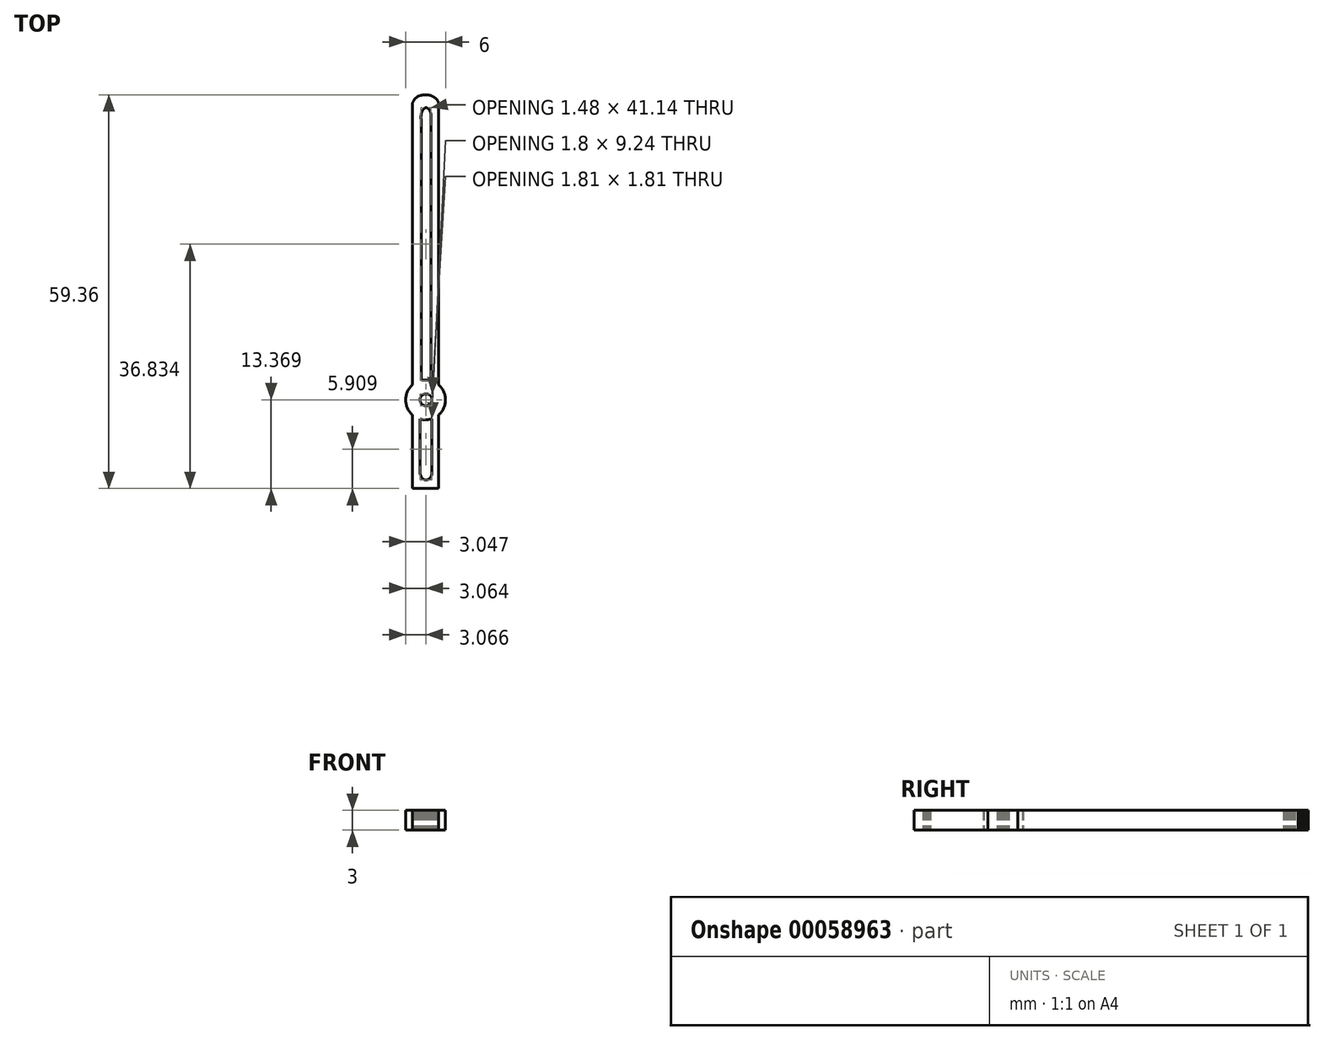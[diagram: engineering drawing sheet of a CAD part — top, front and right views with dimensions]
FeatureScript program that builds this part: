
annotation { "Feature Type Name" : "Feature", "Feature Type Description" : "" }
export const myFeature = defineFeature(function(context is Context, id is Id, definition is map)
    precondition{}
    {
        {
            var Q0;
            Q0=qCreatedBy(makeId("Top.planeOp"),FACE);
            var sketch = newSketch(context, id + "F0", { "sketchPlane" : qUnion([Q0])});
            skLineSegment(sketch, "E0", {"start": v(-1.98, 12.81) * mm, "end": v(-1.98, 28.31) * mm});
            skLineSegment(sketch, "E1", {"start": v(-1.98, 28.31) * mm, "end": v(-1.97, 28.38) * mm});
            skLineSegment(sketch, "E2", {"start": v(-1.97, 28.38) * mm, "end": v(-1.96, 28.45) * mm});
            skLineSegment(sketch, "E3", {"start": v(-1.96, 28.45) * mm, "end": v(-1.94, 28.52) * mm});
            skLineSegment(sketch, "E4", {"start": v(-1.94, 28.52) * mm, "end": v(-1.91, 28.59) * mm});
            skLineSegment(sketch, "E5", {"start": v(-1.91, 28.59) * mm, "end": v(-1.89, 28.65) * mm});
            skLineSegment(sketch, "E6", {"start": v(-1.89, 28.65) * mm, "end": v(-1.86, 28.72) * mm});
            skLineSegment(sketch, "E7", {"start": v(-1.86, 28.72) * mm, "end": v(-1.82, 28.78) * mm});
            skLineSegment(sketch, "E8", {"start": v(-1.82, 28.78) * mm, "end": v(-1.78, 28.85) * mm});
            skLineSegment(sketch, "E9", {"start": v(-1.78, 28.85) * mm, "end": v(-1.74, 28.9) * mm});
            skLineSegment(sketch, "E10", {"start": v(-1.74, 28.9) * mm, "end": v(-1.7, 28.96) * mm});
            skLineSegment(sketch, "E11", {"start": v(-1.7, 28.96) * mm, "end": v(-1.65, 29.02) * mm});
            skLineSegment(sketch, "E12", {"start": v(-1.65, 29.02) * mm, "end": v(-1.6, 29.08) * mm});
            skLineSegment(sketch, "E13", {"start": v(-1.6, 29.08) * mm, "end": v(-1.54, 29.13) * mm});
            skLineSegment(sketch, "E14", {"start": v(-1.54, 29.13) * mm, "end": v(-1.48, 29.18) * mm});
            skLineSegment(sketch, "E15", {"start": v(-1.48, 29.18) * mm, "end": v(-1.42, 29.23) * mm});
            skLineSegment(sketch, "E16", {"start": v(-1.42, 29.23) * mm, "end": v(-1.35, 29.28) * mm});
            skLineSegment(sketch, "E17", {"start": v(-1.35, 29.28) * mm, "end": v(-1.28, 29.32) * mm});
            skLineSegment(sketch, "E18", {"start": v(-1.28, 29.32) * mm, "end": v(-1.21, 29.37) * mm});
            skLineSegment(sketch, "E19", {"start": v(-1.21, 29.37) * mm, "end": v(-1.07, 29.44) * mm});
            skLineSegment(sketch, "E20", {"start": v(-1.07, 29.44) * mm, "end": v(-0.9, 29.51) * mm});
            skLineSegment(sketch, "E21", {"start": v(-0.9, 29.51) * mm, "end": v(-0.74, 29.57) * mm});
            skLineSegment(sketch, "E22", {"start": v(-0.74, 29.57) * mm, "end": v(-0.57, 29.62) * mm});
            skLineSegment(sketch, "E23", {"start": v(-0.57, 29.62) * mm, "end": v(-0.48, 29.63) * mm});
            skLineSegment(sketch, "E24", {"start": v(-0.48, 29.63) * mm, "end": v(-0.38, 29.65) * mm});
            skLineSegment(sketch, "E25", {"start": v(-0.38, 29.65) * mm, "end": v(-0.3, 29.66) * mm});
            skLineSegment(sketch, "E26", {"start": v(-0.3, 29.66) * mm, "end": v(-0.2, 29.67) * mm});
            skLineSegment(sketch, "E27", {"start": v(-0.2, 29.67) * mm, "end": v(-0.1, 29.67) * mm});
            skLineSegment(sketch, "E28", {"start": v(-0.1, 29.67) * mm, "end": v(0, 29.68) * mm});
            skLineSegment(sketch, "E29", {"start": v(0, 29.68) * mm, "end": v(0.1, 29.67) * mm});
            skLineSegment(sketch, "E30", {"start": v(0.1, 29.67) * mm, "end": v(0.2, 29.67) * mm});
            skLineSegment(sketch, "E31", {"start": v(0.2, 29.67) * mm, "end": v(0.3, 29.66) * mm});
            skLineSegment(sketch, "E32", {"start": v(0.3, 29.66) * mm, "end": v(0.4, 29.65) * mm});
            skLineSegment(sketch, "E33", {"start": v(0.4, 29.65) * mm, "end": v(0.5, 29.63) * mm});
            skLineSegment(sketch, "E34", {"start": v(0.5, 29.63) * mm, "end": v(0.59, 29.6) * mm});
            skLineSegment(sketch, "E35", {"start": v(0.59, 29.6) * mm, "end": v(0.68, 29.59) * mm});
            skLineSegment(sketch, "E36", {"start": v(0.68, 29.59) * mm, "end": v(0.77, 29.56) * mm});
            skLineSegment(sketch, "E37", {"start": v(0.77, 29.56) * mm, "end": v(0.86, 29.53) * mm});
            skLineSegment(sketch, "E38", {"start": v(0.86, 29.53) * mm, "end": v(0.94, 29.5) * mm});
            skLineSegment(sketch, "E39", {"start": v(0.94, 29.5) * mm, "end": v(1.02, 29.46) * mm});
            skLineSegment(sketch, "E40", {"start": v(1.02, 29.46) * mm, "end": v(1.1, 29.42) * mm});
            skLineSegment(sketch, "E41", {"start": v(1.1, 29.42) * mm, "end": v(1.18, 29.38) * mm});
            skLineSegment(sketch, "E42", {"start": v(1.18, 29.38) * mm, "end": v(1.26, 29.33) * mm});
            skLineSegment(sketch, "E43", {"start": v(1.26, 29.33) * mm, "end": v(1.33, 29.29) * mm});
            skLineSegment(sketch, "E44", {"start": v(1.33, 29.29) * mm, "end": v(1.4, 29.24) * mm});
            skLineSegment(sketch, "E45", {"start": v(1.4, 29.24) * mm, "end": v(1.46, 29.19) * mm});
            skLineSegment(sketch, "E46", {"start": v(1.46, 29.19) * mm, "end": v(1.53, 29.13) * mm});
            skLineSegment(sketch, "E47", {"start": v(1.53, 29.13) * mm, "end": v(1.59, 29.08) * mm});
            skLineSegment(sketch, "E48", {"start": v(1.59, 29.08) * mm, "end": v(1.64, 29.02) * mm});
            skLineSegment(sketch, "E49", {"start": v(1.64, 29.02) * mm, "end": v(1.7, 28.96) * mm});
            skLineSegment(sketch, "E50", {"start": v(1.7, 28.96) * mm, "end": v(1.74, 28.9) * mm});
            skLineSegment(sketch, "E51", {"start": v(1.74, 28.9) * mm, "end": v(1.78, 28.83) * mm});
            skLineSegment(sketch, "E52", {"start": v(1.78, 28.83) * mm, "end": v(1.82, 28.76) * mm});
            skLineSegment(sketch, "E53", {"start": v(1.82, 28.76) * mm, "end": v(1.86, 28.7) * mm});
            skLineSegment(sketch, "E54", {"start": v(1.86, 28.7) * mm, "end": v(1.9, 28.63) * mm});
            skLineSegment(sketch, "E55", {"start": v(1.9, 28.63) * mm, "end": v(1.92, 28.56) * mm});
            skLineSegment(sketch, "E56", {"start": v(1.92, 28.56) * mm, "end": v(1.94, 28.48) * mm});
            skLineSegment(sketch, "E57", {"start": v(1.94, 28.48) * mm, "end": v(1.96, 28.4) * mm});
            skLineSegment(sketch, "E58", {"start": v(1.96, 28.4) * mm, "end": v(1.97, 28.33) * mm});
            skLineSegment(sketch, "E59", {"start": v(1.97, 28.33) * mm, "end": v(1.98, 28.26) * mm});
            skLineSegment(sketch, "E60", {"start": v(1.98, 28.26) * mm, "end": v(1.98, 28.18) * mm});
            skLineSegment(sketch, "E61", {"start": v(1.98, 28.18) * mm, "end": v(1.98, 28.12) * mm});
            skLineSegment(sketch, "E62", {"start": v(1.98, 28.12) * mm, "end": v(1.98, 12.81) * mm});
            skLineSegment(sketch, "E63", {"start": v(1.98, 12.81) * mm, "end": v(1.98, 5.29) * mm});
            skLineSegment(sketch, "E64", {"start": v(1.98, 5.29) * mm, "end": v(1.98, -7) * mm});
            skLineSegment(sketch, "E65", {"start": v(1.98, -7) * mm, "end": v(1.98, -16.31) * mm});
            skLineSegment(sketch, "E66", {"start": v(1.98, -16.31) * mm, "end": v(1.98, -18.16) * mm});
            skLineSegment(sketch, "E67", {"start": v(1.98, -18.16) * mm, "end": v(1.98, -29.68) * mm});
            skLineSegment(sketch, "E68", {"start": v(1.98, -29.68) * mm, "end": v(-1.98, -29.68) * mm});
            skLineSegment(sketch, "E69", {"start": v(-1.98, -29.68) * mm, "end": v(-1.98, -18.16) * mm});
            skLineSegment(sketch, "E70", {"start": v(-1.98, -18.16) * mm, "end": v(-1.98, -16.31) * mm});
            skLineSegment(sketch, "E71", {"start": v(-1.98, -16.31) * mm, "end": v(-1.98, -7) * mm});
            skLineSegment(sketch, "E72", {"start": v(-1.98, -7) * mm, "end": v(-1.98, 5.26) * mm});
            skLineSegment(sketch, "E73", {"start": v(-1.98, 5.26) * mm, "end": v(-1.98, 12.81) * mm});
            skLineSegment(sketch, "E74", {"start": v(0.97, -16.31) * mm, "end": v(0.97, -16.25) * mm});
            skLineSegment(sketch, "E75", {"start": v(0.97, -16.25) * mm, "end": v(0.96, -16.2) * mm});
            skLineSegment(sketch, "E76", {"start": v(0.96, -16.2) * mm, "end": v(0.95, -16.14) * mm});
            skLineSegment(sketch, "E77", {"start": v(0.95, -16.14) * mm, "end": v(0.94, -16.09) * mm});
            skLineSegment(sketch, "E78", {"start": v(0.94, -16.09) * mm, "end": v(0.93, -16.03) * mm});
            skLineSegment(sketch, "E79", {"start": v(0.93, -16.03) * mm, "end": v(0.9, -15.98) * mm});
            skLineSegment(sketch, "E80", {"start": v(0.9, -15.98) * mm, "end": v(0.88, -15.93) * mm});
            skLineSegment(sketch, "E81", {"start": v(0.88, -15.93) * mm, "end": v(0.86, -15.88) * mm});
            skLineSegment(sketch, "E82", {"start": v(0.86, -15.88) * mm, "end": v(0.83, -15.83) * mm});
            skLineSegment(sketch, "E83", {"start": v(0.83, -15.83) * mm, "end": v(0.8, -15.78) * mm});
            skLineSegment(sketch, "E84", {"start": v(0.8, -15.78) * mm, "end": v(0.76, -15.74) * mm});
            skLineSegment(sketch, "E85", {"start": v(0.76, -15.74) * mm, "end": v(0.72, -15.7) * mm});
            skLineSegment(sketch, "E86", {"start": v(0.72, -15.7) * mm, "end": v(0.68, -15.65) * mm});
            skLineSegment(sketch, "E87", {"start": v(0.68, -15.65) * mm, "end": v(0.64, -15.61) * mm});
            skLineSegment(sketch, "E88", {"start": v(0.64, -15.61) * mm, "end": v(0.6, -15.58) * mm});
            skLineSegment(sketch, "E89", {"start": v(0.6, -15.58) * mm, "end": v(0.55, -15.55) * mm});
            skLineSegment(sketch, "E90", {"start": v(0.55, -15.55) * mm, "end": v(0.5, -15.52) * mm});
            skLineSegment(sketch, "E91", {"start": v(0.5, -15.52) * mm, "end": v(0.45, -15.5) * mm});
            skLineSegment(sketch, "E92", {"start": v(0.45, -15.5) * mm, "end": v(0.4, -15.47) * mm});
            skLineSegment(sketch, "E93", {"start": v(0.4, -15.47) * mm, "end": v(0.35, -15.45) * mm});
            skLineSegment(sketch, "E94", {"start": v(0.35, -15.45) * mm, "end": v(0.3, -15.44) * mm});
            skLineSegment(sketch, "E95", {"start": v(0.3, -15.44) * mm, "end": v(0.24, -15.42) * mm});
            skLineSegment(sketch, "E96", {"start": v(0.24, -15.42) * mm, "end": v(0.18, -15.41) * mm});
            skLineSegment(sketch, "E97", {"start": v(0.18, -15.41) * mm, "end": v(0.12, -15.4) * mm});
            skLineSegment(sketch, "E98", {"start": v(0.12, -15.4) * mm, "end": v(0.07, -15.4) * mm});
            skLineSegment(sketch, "E99", {"start": v(0.07, -15.4) * mm, "end": v(0, -15.4) * mm});
            skLineSegment(sketch, "E100", {"start": v(0, -15.4) * mm, "end": v(-0.05, -15.41) * mm});
            skLineSegment(sketch, "E101", {"start": v(-0.05, -15.41) * mm, "end": v(-0.1, -15.42) * mm});
            skLineSegment(sketch, "E102", {"start": v(-0.1, -15.42) * mm, "end": v(-0.16, -15.43) * mm});
            skLineSegment(sketch, "E103", {"start": v(-0.16, -15.43) * mm, "end": v(-0.21, -15.45) * mm});
            skLineSegment(sketch, "E104", {"start": v(-0.21, -15.45) * mm, "end": v(-0.27, -15.47) * mm});
            skLineSegment(sketch, "E105", {"start": v(-0.27, -15.47) * mm, "end": v(-0.32, -15.5) * mm});
            skLineSegment(sketch, "E106", {"start": v(-0.32, -15.5) * mm, "end": v(-0.37, -15.52) * mm});
            skLineSegment(sketch, "E107", {"start": v(-0.37, -15.52) * mm, "end": v(-0.42, -15.55) * mm});
            skLineSegment(sketch, "E108", {"start": v(-0.42, -15.55) * mm, "end": v(-0.46, -15.58) * mm});
            skLineSegment(sketch, "E109", {"start": v(-0.46, -15.58) * mm, "end": v(-0.5, -15.61) * mm});
            skLineSegment(sketch, "E110", {"start": v(-0.5, -15.61) * mm, "end": v(-0.55, -15.65) * mm});
            skLineSegment(sketch, "E111", {"start": v(-0.55, -15.65) * mm, "end": v(-0.6, -15.69) * mm});
            skLineSegment(sketch, "E112", {"start": v(-0.6, -15.69) * mm, "end": v(-0.63, -15.73) * mm});
            skLineSegment(sketch, "E113", {"start": v(-0.63, -15.73) * mm, "end": v(-0.67, -15.78) * mm});
            skLineSegment(sketch, "E114", {"start": v(-0.67, -15.78) * mm, "end": v(-0.7, -15.82) * mm});
            skLineSegment(sketch, "E115", {"start": v(-0.7, -15.82) * mm, "end": v(-0.73, -15.87) * mm});
            skLineSegment(sketch, "E116", {"start": v(-0.73, -15.87) * mm, "end": v(-0.75, -15.92) * mm});
            skLineSegment(sketch, "E117", {"start": v(-0.75, -15.92) * mm, "end": v(-0.78, -15.97) * mm});
            skLineSegment(sketch, "E118", {"start": v(-0.78, -15.97) * mm, "end": v(-0.8, -16.03) * mm});
            skLineSegment(sketch, "E119", {"start": v(-0.8, -16.03) * mm, "end": v(-0.81, -16.08) * mm});
            skLineSegment(sketch, "E120", {"start": v(-0.81, -16.08) * mm, "end": v(-0.82, -16.14) * mm});
            skLineSegment(sketch, "E121", {"start": v(-0.82, -16.14) * mm, "end": v(-0.83, -16.2) * mm});
            skLineSegment(sketch, "E122", {"start": v(-0.83, -16.2) * mm, "end": v(-0.84, -16.25) * mm});
            skLineSegment(sketch, "E123", {"start": v(-0.84, -16.25) * mm, "end": v(-0.84, -16.3) * mm});
            skLineSegment(sketch, "E124", {"start": v(-0.84, -16.3) * mm, "end": v(-0.84, -16.36) * mm});
            skLineSegment(sketch, "E125", {"start": v(-0.84, -16.36) * mm, "end": v(-0.83, -16.42) * mm});
            skLineSegment(sketch, "E126", {"start": v(-0.83, -16.42) * mm, "end": v(-0.83, -16.48) * mm});
            skLineSegment(sketch, "E127", {"start": v(-0.83, -16.48) * mm, "end": v(-0.81, -16.53) * mm});
            skLineSegment(sketch, "E128", {"start": v(-0.81, -16.53) * mm, "end": v(-0.8, -16.59) * mm});
            skLineSegment(sketch, "E129", {"start": v(-0.8, -16.59) * mm, "end": v(-0.78, -16.64) * mm});
            skLineSegment(sketch, "E130", {"start": v(-0.78, -16.64) * mm, "end": v(-0.76, -16.7) * mm});
            skLineSegment(sketch, "E131", {"start": v(-0.76, -16.7) * mm, "end": v(-0.73, -16.74) * mm});
            skLineSegment(sketch, "E132", {"start": v(-0.73, -16.74) * mm, "end": v(-0.7, -16.8) * mm});
            skLineSegment(sketch, "E133", {"start": v(-0.7, -16.8) * mm, "end": v(-0.67, -16.84) * mm});
            skLineSegment(sketch, "E134", {"start": v(-0.67, -16.84) * mm, "end": v(-0.64, -16.88) * mm});
            skLineSegment(sketch, "E135", {"start": v(-0.64, -16.88) * mm, "end": v(-0.6, -16.93) * mm});
            skLineSegment(sketch, "E136", {"start": v(-0.6, -16.93) * mm, "end": v(-0.56, -16.97) * mm});
            skLineSegment(sketch, "E137", {"start": v(-0.56, -16.97) * mm, "end": v(-0.52, -17) * mm});
            skLineSegment(sketch, "E138", {"start": v(-0.52, -17) * mm, "end": v(-0.47, -17.04) * mm});
            skLineSegment(sketch, "E139", {"start": v(-0.47, -17.04) * mm, "end": v(-0.43, -17.07) * mm});
            skLineSegment(sketch, "E140", {"start": v(-0.43, -17.07) * mm, "end": v(-0.38, -17.1) * mm});
            skLineSegment(sketch, "E141", {"start": v(-0.38, -17.1) * mm, "end": v(-0.33, -17.13) * mm});
            skLineSegment(sketch, "E142", {"start": v(-0.33, -17.13) * mm, "end": v(-0.27, -17.15) * mm});
            skLineSegment(sketch, "E143", {"start": v(-0.27, -17.15) * mm, "end": v(-0.22, -17.17) * mm});
            skLineSegment(sketch, "E144", {"start": v(-0.22, -17.17) * mm, "end": v(-0.17, -17.19) * mm});
            skLineSegment(sketch, "E145", {"start": v(-0.17, -17.19) * mm, "end": v(-0.11, -17.2) * mm});
            skLineSegment(sketch, "E146", {"start": v(-0.11, -17.2) * mm, "end": v(-0.06, -17.2) * mm});
            skLineSegment(sketch, "E147", {"start": v(-0.06, -17.2) * mm, "end": v(0, -17.21) * mm});
            skLineSegment(sketch, "E148", {"start": v(0, -17.21) * mm, "end": v(0.06, -17.22) * mm});
            skLineSegment(sketch, "E149", {"start": v(0.06, -17.22) * mm, "end": v(0.11, -17.21) * mm});
            skLineSegment(sketch, "E150", {"start": v(0.11, -17.21) * mm, "end": v(0.17, -17.21) * mm});
            skLineSegment(sketch, "E151", {"start": v(0.17, -17.21) * mm, "end": v(0.23, -17.2) * mm});
            skLineSegment(sketch, "E152", {"start": v(0.23, -17.2) * mm, "end": v(0.28, -17.19) * mm});
            skLineSegment(sketch, "E153", {"start": v(0.28, -17.19) * mm, "end": v(0.34, -17.17) * mm});
            skLineSegment(sketch, "E154", {"start": v(0.34, -17.17) * mm, "end": v(0.4, -17.16) * mm});
            skLineSegment(sketch, "E155", {"start": v(0.4, -17.16) * mm, "end": v(0.44, -17.13) * mm});
            skLineSegment(sketch, "E156", {"start": v(0.44, -17.13) * mm, "end": v(0.5, -17.1) * mm});
            skLineSegment(sketch, "E157", {"start": v(0.5, -17.1) * mm, "end": v(0.54, -17.08) * mm});
            skLineSegment(sketch, "E158", {"start": v(0.54, -17.08) * mm, "end": v(0.6, -17.05) * mm});
            skLineSegment(sketch, "E159", {"start": v(0.6, -17.05) * mm, "end": v(0.64, -17.01) * mm});
            skLineSegment(sketch, "E160", {"start": v(0.64, -17.01) * mm, "end": v(0.68, -16.98) * mm});
            skLineSegment(sketch, "E161", {"start": v(0.68, -16.98) * mm, "end": v(0.72, -16.94) * mm});
            skLineSegment(sketch, "E162", {"start": v(0.72, -16.94) * mm, "end": v(0.76, -16.9) * mm});
            skLineSegment(sketch, "E163", {"start": v(0.76, -16.9) * mm, "end": v(0.8, -16.85) * mm});
            skLineSegment(sketch, "E164", {"start": v(0.8, -16.85) * mm, "end": v(0.82, -16.8) * mm});
            skLineSegment(sketch, "E165", {"start": v(0.82, -16.8) * mm, "end": v(0.85, -16.75) * mm});
            skLineSegment(sketch, "E166", {"start": v(0.85, -16.75) * mm, "end": v(0.88, -16.7) * mm});
            skLineSegment(sketch, "E167", {"start": v(0.88, -16.7) * mm, "end": v(0.9, -16.65) * mm});
            skLineSegment(sketch, "E168", {"start": v(0.9, -16.65) * mm, "end": v(0.92, -16.6) * mm});
            skLineSegment(sketch, "E169", {"start": v(0.92, -16.6) * mm, "end": v(0.94, -16.54) * mm});
            skLineSegment(sketch, "E170", {"start": v(0.94, -16.54) * mm, "end": v(0.95, -16.49) * mm});
            skLineSegment(sketch, "E171", {"start": v(0.95, -16.49) * mm, "end": v(0.96, -16.43) * mm});
            skLineSegment(sketch, "E172", {"start": v(0.96, -16.43) * mm, "end": v(0.97, -16.38) * mm});
            skLineSegment(sketch, "E173", {"start": v(0.97, -16.38) * mm, "end": v(0.97, -16.31) * mm});
            skLineSegment(sketch, "E174", {"start": v(-0.83, -27.22) * mm, "end": v(-0.83, -27.34) * mm});
            skLineSegment(sketch, "E175", {"start": v(-0.83, -27.34) * mm, "end": v(-0.81, -27.46) * mm});
            skLineSegment(sketch, "E176", {"start": v(-0.81, -27.46) * mm, "end": v(-0.8, -27.57) * mm});
            skLineSegment(sketch, "E177", {"start": v(-0.8, -27.57) * mm, "end": v(-0.76, -27.68) * mm});
            skLineSegment(sketch, "E178", {"start": v(-0.76, -27.68) * mm, "end": v(-0.72, -27.78) * mm});
            skLineSegment(sketch, "E179", {"start": v(-0.72, -27.78) * mm, "end": v(-0.68, -27.87) * mm});
            skLineSegment(sketch, "E180", {"start": v(-0.68, -27.87) * mm, "end": v(-0.63, -27.96) * mm});
            skLineSegment(sketch, "E181", {"start": v(-0.63, -27.96) * mm, "end": v(-0.57, -28.05) * mm});
            skLineSegment(sketch, "E182", {"start": v(-0.57, -28.05) * mm, "end": v(-0.5, -28.12) * mm});
            skLineSegment(sketch, "E183", {"start": v(-0.5, -28.12) * mm, "end": v(-0.44, -28.2) * mm});
            skLineSegment(sketch, "E184", {"start": v(-0.44, -28.2) * mm, "end": v(-0.36, -28.25) * mm});
            skLineSegment(sketch, "E185", {"start": v(-0.36, -28.25) * mm, "end": v(-0.28, -28.3) * mm});
            skLineSegment(sketch, "E186", {"start": v(-0.28, -28.3) * mm, "end": v(-0.2, -28.34) * mm});
            skLineSegment(sketch, "E187", {"start": v(-0.2, -28.34) * mm, "end": v(-0.12, -28.37) * mm});
            skLineSegment(sketch, "E188", {"start": v(-0.12, -28.37) * mm, "end": v(-0.07, -28.38) * mm});
            skLineSegment(sketch, "E189", {"start": v(-0.07, -28.38) * mm, "end": v(-0.03, -28.38) * mm});
            skLineSegment(sketch, "E190", {"start": v(-0.03, -28.38) * mm, "end": v(0.02, -28.39) * mm});
            skLineSegment(sketch, "E191", {"start": v(0.02, -28.39) * mm, "end": v(0.07, -28.4) * mm});
            skLineSegment(sketch, "E192", {"start": v(0.07, -28.4) * mm, "end": v(0.11, -28.39) * mm});
            skLineSegment(sketch, "E193", {"start": v(0.11, -28.39) * mm, "end": v(0.16, -28.38) * mm});
            skLineSegment(sketch, "E194", {"start": v(0.16, -28.38) * mm, "end": v(0.2, -28.38) * mm});
            skLineSegment(sketch, "E195", {"start": v(0.2, -28.38) * mm, "end": v(0.25, -28.37) * mm});
            skLineSegment(sketch, "E196", {"start": v(0.25, -28.37) * mm, "end": v(0.33, -28.34) * mm});
            skLineSegment(sketch, "E197", {"start": v(0.33, -28.34) * mm, "end": v(0.41, -28.3) * mm});
            skLineSegment(sketch, "E198", {"start": v(0.41, -28.3) * mm, "end": v(0.5, -28.25) * mm});
            skLineSegment(sketch, "E199", {"start": v(0.5, -28.25) * mm, "end": v(0.57, -28.2) * mm});
            skLineSegment(sketch, "E200", {"start": v(0.57, -28.2) * mm, "end": v(0.64, -28.12) * mm});
            skLineSegment(sketch, "E201", {"start": v(0.64, -28.12) * mm, "end": v(0.7, -28.05) * mm});
            skLineSegment(sketch, "E202", {"start": v(0.7, -28.05) * mm, "end": v(0.76, -27.96) * mm});
            skLineSegment(sketch, "E203", {"start": v(0.76, -27.96) * mm, "end": v(0.8, -27.87) * mm});
            skLineSegment(sketch, "E204", {"start": v(0.8, -27.87) * mm, "end": v(0.85, -27.78) * mm});
            skLineSegment(sketch, "E205", {"start": v(0.85, -27.78) * mm, "end": v(0.9, -27.68) * mm});
            skLineSegment(sketch, "E206", {"start": v(0.9, -27.68) * mm, "end": v(0.92, -27.57) * mm});
            skLineSegment(sketch, "E207", {"start": v(0.92, -27.57) * mm, "end": v(0.94, -27.46) * mm});
            skLineSegment(sketch, "E208", {"start": v(0.94, -27.46) * mm, "end": v(0.96, -27.34) * mm});
            skLineSegment(sketch, "E209", {"start": v(0.96, -27.34) * mm, "end": v(0.96, -27.22) * mm});
            skLineSegment(sketch, "E210", {"start": v(0.96, -27.22) * mm, "end": v(0.96, -19) * mm});
            skLineSegment(sketch, "E211", {"start": v(0.96, -19) * mm, "end": v(0.96, -18.89) * mm});
            skLineSegment(sketch, "E212", {"start": v(0.96, -18.89) * mm, "end": v(0.95, -18.77) * mm});
            skLineSegment(sketch, "E213", {"start": v(0.95, -18.77) * mm, "end": v(0.92, -18.66) * mm});
            skLineSegment(sketch, "E214", {"start": v(0.92, -18.66) * mm, "end": v(0.9, -18.55) * mm});
            skLineSegment(sketch, "E215", {"start": v(0.9, -18.55) * mm, "end": v(0.86, -18.45) * mm});
            skLineSegment(sketch, "E216", {"start": v(0.86, -18.45) * mm, "end": v(0.81, -18.35) * mm});
            skLineSegment(sketch, "E217", {"start": v(0.81, -18.35) * mm, "end": v(0.76, -18.26) * mm});
            skLineSegment(sketch, "E218", {"start": v(0.76, -18.26) * mm, "end": v(0.7, -18.18) * mm});
            skLineSegment(sketch, "E219", {"start": v(0.7, -18.18) * mm, "end": v(0.64, -18.1) * mm});
            skLineSegment(sketch, "E220", {"start": v(0.64, -18.1) * mm, "end": v(0.57, -18.04) * mm});
            skLineSegment(sketch, "E221", {"start": v(0.57, -18.04) * mm, "end": v(0.5, -17.98) * mm});
            skLineSegment(sketch, "E222", {"start": v(0.5, -17.98) * mm, "end": v(0.42, -17.93) * mm});
            skLineSegment(sketch, "E223", {"start": v(0.42, -17.93) * mm, "end": v(0.33, -17.89) * mm});
            skLineSegment(sketch, "E224", {"start": v(0.33, -17.89) * mm, "end": v(0.25, -17.86) * mm});
            skLineSegment(sketch, "E225", {"start": v(0.25, -17.86) * mm, "end": v(0.2, -17.85) * mm});
            skLineSegment(sketch, "E226", {"start": v(0.2, -17.85) * mm, "end": v(0.16, -17.84) * mm});
            skLineSegment(sketch, "E227", {"start": v(0.16, -17.84) * mm, "end": v(0.11, -17.84) * mm});
            skLineSegment(sketch, "E228", {"start": v(0.11, -17.84) * mm, "end": v(0.07, -17.84) * mm});
            skLineSegment(sketch, "E229", {"start": v(0.07, -17.84) * mm, "end": v(0.02, -17.84) * mm});
            skLineSegment(sketch, "E230", {"start": v(0.02, -17.84) * mm, "end": v(-0.03, -17.84) * mm});
            skLineSegment(sketch, "E231", {"start": v(-0.03, -17.84) * mm, "end": v(-0.07, -17.85) * mm});
            skLineSegment(sketch, "E232", {"start": v(-0.07, -17.85) * mm, "end": v(-0.12, -17.86) * mm});
            skLineSegment(sketch, "E233", {"start": v(-0.12, -17.86) * mm, "end": v(-0.2, -17.89) * mm});
            skLineSegment(sketch, "E234", {"start": v(-0.2, -17.89) * mm, "end": v(-0.28, -17.93) * mm});
            skLineSegment(sketch, "E235", {"start": v(-0.28, -17.93) * mm, "end": v(-0.36, -17.98) * mm});
            skLineSegment(sketch, "E236", {"start": v(-0.36, -17.98) * mm, "end": v(-0.44, -18.04) * mm});
            skLineSegment(sketch, "E237", {"start": v(-0.44, -18.04) * mm, "end": v(-0.5, -18.1) * mm});
            skLineSegment(sketch, "E238", {"start": v(-0.5, -18.1) * mm, "end": v(-0.57, -18.18) * mm});
            skLineSegment(sketch, "E239", {"start": v(-0.57, -18.18) * mm, "end": v(-0.63, -18.26) * mm});
            skLineSegment(sketch, "E240", {"start": v(-0.63, -18.26) * mm, "end": v(-0.68, -18.35) * mm});
            skLineSegment(sketch, "E241", {"start": v(-0.68, -18.35) * mm, "end": v(-0.72, -18.45) * mm});
            skLineSegment(sketch, "E242", {"start": v(-0.72, -18.45) * mm, "end": v(-0.76, -18.55) * mm});
            skLineSegment(sketch, "E243", {"start": v(-0.76, -18.55) * mm, "end": v(-0.8, -18.66) * mm});
            skLineSegment(sketch, "E244", {"start": v(-0.8, -18.66) * mm, "end": v(-0.81, -18.77) * mm});
            skLineSegment(sketch, "E245", {"start": v(-0.81, -18.77) * mm, "end": v(-0.83, -18.89) * mm});
            skLineSegment(sketch, "E246", {"start": v(-0.83, -18.89) * mm, "end": v(-0.83, -19) * mm});
            skLineSegment(sketch, "E247", {"start": v(-0.83, -19) * mm, "end": v(-0.83, -27.22) * mm});
            skLineSegment(sketch, "E248", {"start": v(-0.67, 11.1) * mm, "end": v(-0.67, 25.9) * mm});
            skLineSegment(sketch, "E249", {"start": v(-0.67, 25.9) * mm, "end": v(-0.68, 26) * mm});
            skLineSegment(sketch, "E250", {"start": v(-0.68, 26) * mm, "end": v(-0.69, 26.1) * mm});
            skLineSegment(sketch, "E251", {"start": v(-0.69, 26.1) * mm, "end": v(-0.7, 26.19) * mm});
            skLineSegment(sketch, "E252", {"start": v(-0.7, 26.19) * mm, "end": v(-0.7, 26.29) * mm});
            skLineSegment(sketch, "E253", {"start": v(-0.7, 26.29) * mm, "end": v(-0.7, 26.44) * mm});
            skLineSegment(sketch, "E254", {"start": v(-0.7, 26.44) * mm, "end": v(-0.68, 26.58) * mm});
            skLineSegment(sketch, "E255", {"start": v(-0.68, 26.58) * mm, "end": v(-0.66, 26.72) * mm});
            skLineSegment(sketch, "E256", {"start": v(-0.66, 26.72) * mm, "end": v(-0.63, 26.85) * mm});
            skLineSegment(sketch, "E257", {"start": v(-0.63, 26.85) * mm, "end": v(-0.6, 26.97) * mm});
            skLineSegment(sketch, "E258", {"start": v(-0.6, 26.97) * mm, "end": v(-0.56, 27.1) * mm});
            skLineSegment(sketch, "E259", {"start": v(-0.56, 27.1) * mm, "end": v(-0.52, 27.2) * mm});
            skLineSegment(sketch, "E260", {"start": v(-0.52, 27.2) * mm, "end": v(-0.47, 27.3) * mm});
            skLineSegment(sketch, "E261", {"start": v(-0.47, 27.3) * mm, "end": v(-0.41, 27.4) * mm});
            skLineSegment(sketch, "E262", {"start": v(-0.41, 27.4) * mm, "end": v(-0.35, 27.48) * mm});
            skLineSegment(sketch, "E263", {"start": v(-0.35, 27.48) * mm, "end": v(-0.3, 27.55) * mm});
            skLineSegment(sketch, "E264", {"start": v(-0.3, 27.55) * mm, "end": v(-0.22, 27.61) * mm});
            skLineSegment(sketch, "E265", {"start": v(-0.22, 27.61) * mm, "end": v(-0.15, 27.66) * mm});
            skLineSegment(sketch, "E266", {"start": v(-0.15, 27.66) * mm, "end": v(-0.08, 27.7) * mm});
            skLineSegment(sketch, "E267", {"start": v(-0.08, 27.7) * mm, "end": v(-0.04, 27.7) * mm});
            skLineSegment(sketch, "E268", {"start": v(-0.04, 27.7) * mm, "end": v(0, 27.72) * mm});
            skLineSegment(sketch, "E269", {"start": v(0, 27.72) * mm, "end": v(0.04, 27.72) * mm});
            skLineSegment(sketch, "E270", {"start": v(0.04, 27.72) * mm, "end": v(0.08, 27.72) * mm});
            skLineSegment(sketch, "E271", {"start": v(0.08, 27.72) * mm, "end": v(0.14, 27.72) * mm});
            skLineSegment(sketch, "E272", {"start": v(0.14, 27.72) * mm, "end": v(0.2, 27.7) * mm});
            skLineSegment(sketch, "E273", {"start": v(0.2, 27.7) * mm, "end": v(0.25, 27.69) * mm});
            skLineSegment(sketch, "E274", {"start": v(0.25, 27.69) * mm, "end": v(0.3, 27.66) * mm});
            skLineSegment(sketch, "E275", {"start": v(0.3, 27.66) * mm, "end": v(0.36, 27.63) * mm});
            skLineSegment(sketch, "E276", {"start": v(0.36, 27.63) * mm, "end": v(0.41, 27.58) * mm});
            skLineSegment(sketch, "E277", {"start": v(0.41, 27.58) * mm, "end": v(0.46, 27.54) * mm});
            skLineSegment(sketch, "E278", {"start": v(0.46, 27.54) * mm, "end": v(0.5, 27.48) * mm});
            skLineSegment(sketch, "E279", {"start": v(0.5, 27.48) * mm, "end": v(0.55, 27.42) * mm});
            skLineSegment(sketch, "E280", {"start": v(0.55, 27.42) * mm, "end": v(0.6, 27.35) * mm});
            skLineSegment(sketch, "E281", {"start": v(0.6, 27.35) * mm, "end": v(0.64, 27.28) * mm});
            skLineSegment(sketch, "E282", {"start": v(0.64, 27.28) * mm, "end": v(0.67, 27.2) * mm});
            skLineSegment(sketch, "E283", {"start": v(0.67, 27.2) * mm, "end": v(0.7, 27.12) * mm});
            skLineSegment(sketch, "E284", {"start": v(0.7, 27.12) * mm, "end": v(0.74, 27.04) * mm});
            skLineSegment(sketch, "E285", {"start": v(0.74, 27.04) * mm, "end": v(0.77, 26.95) * mm});
            skLineSegment(sketch, "E286", {"start": v(0.77, 26.95) * mm, "end": v(0.79, 26.85) * mm});
            skLineSegment(sketch, "E287", {"start": v(0.79, 26.85) * mm, "end": v(0.79, 11.1) * mm});
            skLineSegment(sketch, "E288", {"start": v(0.79, 11.1) * mm, "end": v(0.79, 2.74) * mm});
            skLineSegment(sketch, "E289", {"start": v(0.79, 2.74) * mm, "end": v(0.79, -13.26) * mm});
            skLineSegment(sketch, "E290", {"start": v(0.79, -13.26) * mm, "end": v(0.79, -13.29) * mm});
            skLineSegment(sketch, "E291", {"start": v(0.79, -13.29) * mm, "end": v(0.79, -13.44) * mm});
            skLineSegment(sketch, "E292", {"start": v(0.79, -13.44) * mm, "end": v(0.77, -13.58) * mm});
            skLineSegment(sketch, "E293", {"start": v(0.77, -13.58) * mm, "end": v(0.76, -13.71) * mm});
            skLineSegment(sketch, "E294", {"start": v(0.76, -13.71) * mm, "end": v(0.73, -13.84) * mm});
            skLineSegment(sketch, "E295", {"start": v(0.73, -13.84) * mm, "end": v(0.7, -13.97) * mm});
            skLineSegment(sketch, "E296", {"start": v(0.7, -13.97) * mm, "end": v(0.66, -14.08) * mm});
            skLineSegment(sketch, "E297", {"start": v(0.66, -14.08) * mm, "end": v(0.62, -14.2) * mm});
            skLineSegment(sketch, "E298", {"start": v(0.62, -14.2) * mm, "end": v(0.57, -14.3) * mm});
            skLineSegment(sketch, "E299", {"start": v(0.57, -14.3) * mm, "end": v(0.52, -14.39) * mm});
            skLineSegment(sketch, "E300", {"start": v(0.52, -14.39) * mm, "end": v(0.47, -14.47) * mm});
            skLineSegment(sketch, "E301", {"start": v(0.47, -14.47) * mm, "end": v(0.4, -14.54) * mm});
            skLineSegment(sketch, "E302", {"start": v(0.4, -14.54) * mm, "end": v(0.34, -14.6) * mm});
            skLineSegment(sketch, "E303", {"start": v(0.34, -14.6) * mm, "end": v(0.28, -14.64) * mm});
            skLineSegment(sketch, "E304", {"start": v(0.28, -14.64) * mm, "end": v(0.2, -14.68) * mm});
            skLineSegment(sketch, "E305", {"start": v(0.2, -14.68) * mm, "end": v(0.14, -14.7) * mm});
            skLineSegment(sketch, "E306", {"start": v(0.14, -14.7) * mm, "end": v(0.06, -14.7) * mm});
            skLineSegment(sketch, "E307", {"start": v(0.06, -14.7) * mm, "end": v(-0.01, -14.7) * mm});
            skLineSegment(sketch, "E308", {"start": v(-0.01, -14.7) * mm, "end": v(-0.08, -14.68) * mm});
            skLineSegment(sketch, "E309", {"start": v(-0.08, -14.68) * mm, "end": v(-0.15, -14.64) * mm});
            skLineSegment(sketch, "E310", {"start": v(-0.15, -14.64) * mm, "end": v(-0.22, -14.6) * mm});
            skLineSegment(sketch, "E311", {"start": v(-0.22, -14.6) * mm, "end": v(-0.28, -14.54) * mm});
            skLineSegment(sketch, "E312", {"start": v(-0.28, -14.54) * mm, "end": v(-0.34, -14.47) * mm});
            skLineSegment(sketch, "E313", {"start": v(-0.34, -14.47) * mm, "end": v(-0.4, -14.4) * mm});
            skLineSegment(sketch, "E314", {"start": v(-0.4, -14.4) * mm, "end": v(-0.44, -14.3) * mm});
            skLineSegment(sketch, "E315", {"start": v(-0.44, -14.3) * mm, "end": v(-0.5, -14.2) * mm});
            skLineSegment(sketch, "E316", {"start": v(-0.5, -14.2) * mm, "end": v(-0.53, -14.1) * mm});
            skLineSegment(sketch, "E317", {"start": v(-0.53, -14.1) * mm, "end": v(-0.57, -13.98) * mm});
            skLineSegment(sketch, "E318", {"start": v(-0.57, -13.98) * mm, "end": v(-0.6, -13.86) * mm});
            skLineSegment(sketch, "E319", {"start": v(-0.6, -13.86) * mm, "end": v(-0.63, -13.74) * mm});
            skLineSegment(sketch, "E320", {"start": v(-0.63, -13.74) * mm, "end": v(-0.65, -13.6) * mm});
            skLineSegment(sketch, "E321", {"start": v(-0.65, -13.6) * mm, "end": v(-0.66, -13.46) * mm});
            skLineSegment(sketch, "E322", {"start": v(-0.66, -13.46) * mm, "end": v(-0.67, -13.32) * mm});
            skLineSegment(sketch, "E323", {"start": v(-0.67, -13.32) * mm, "end": v(-0.67, 2.73) * mm});
            skLineSegment(sketch, "E324", {"start": v(-0.67, 2.73) * mm, "end": v(-0.67, 11.1) * mm});
            skLineSegment(sketch, "E325", {"start": v(-1.98, -16.31) * mm, "end": v(1.98, -16.31) * mm, "construction": true});
            skPoint(sketch, "E326", {"position": v(0, -16.31) * mm});
            skCircle(sketch, "E327", {"center": v(0, -16.31) * mm, "radius": 3 * mm});
            skSolve(sketch);
        }
        {
            var Q0;
            Q0=makeQuery(id+"F0.imprint","IMPRINT",FACE,{"disambiguationData":[TD([[makeQuery(id+"F0.imprint","IMPRINT",EDGE,{"derivedFrom":sQuery(id+"F0.wireOp",EDGE,"E0")}),-1.0]])]});
            var Q1;
            {var subQ0=sQuery(id+"F0.wireOp",EDGE,"E66");Q1=makeQuery(id+"F0.imprint","IMPRINT",FACE,{"disambiguationData":[TD([[makeQuery(id+"F0.imprint","IMPRINT",EDGE,{"derivedFrom":subQ0}),1.0]])]});}
            var Q2;
            {var subQ1=sQuery(id+"F0.wireOp",EDGE,"E66");Q2=makeQuery(id+"F0.imprint","IMPRINT",FACE,{"disambiguationData":[TD([[makeQuery(id+"F0.imprint","IMPRINT",EDGE,{"derivedFrom":subQ1}),-1.0]])]});}
            var Q3;
            {var subQ0=sQuery(id+"F0.wireOp",EDGE,"E70");Q3=makeQuery(id+"F0.imprint","IMPRINT",FACE,{"disambiguationData":[TD([[makeQuery(id+"F0.imprint","IMPRINT",EDGE,{"derivedFrom":subQ0}),1.0]])]});}
            var Q4;
            {var subQ2=sQuery(id+"F0.wireOp",EDGE,"E68");Q4=makeQuery(id+"F0.imprint","IMPRINT",FACE,{"disambiguationData":[TD([[makeQuery(id+"F0.imprint","IMPRINT",EDGE,{"derivedFrom":subQ2}),-1.0]])]});}
            var Q5;
            {var subQ0=sQuery(id+"F0.wireOp",EDGE,"E292");Q5=makeQuery(id+"F0.imprint","IMPRINT",FACE,{"disambiguationData":[TD([[makeQuery(id+"F0.imprint","IMPRINT",EDGE,{"derivedFrom":subQ0}),-1.0]])]});}
            var Q6;
            {var subQ5=sQuery(id+"F0.wireOp",EDGE,"E211");Q6=makeQuery(id+"F0.imprint","IMPRINT",FACE,{"disambiguationData":[TD([[makeQuery(id+"F0.imprint","IMPRINT",EDGE,{"derivedFrom":subQ5}),1.0]])]});}
            extrude(context, id + "F1", {"entities" : qUnion([Q0, Q1, Q2, Q3, Q4, Q5, Q6]), "depth" : 3 * mm});
        }
    });
